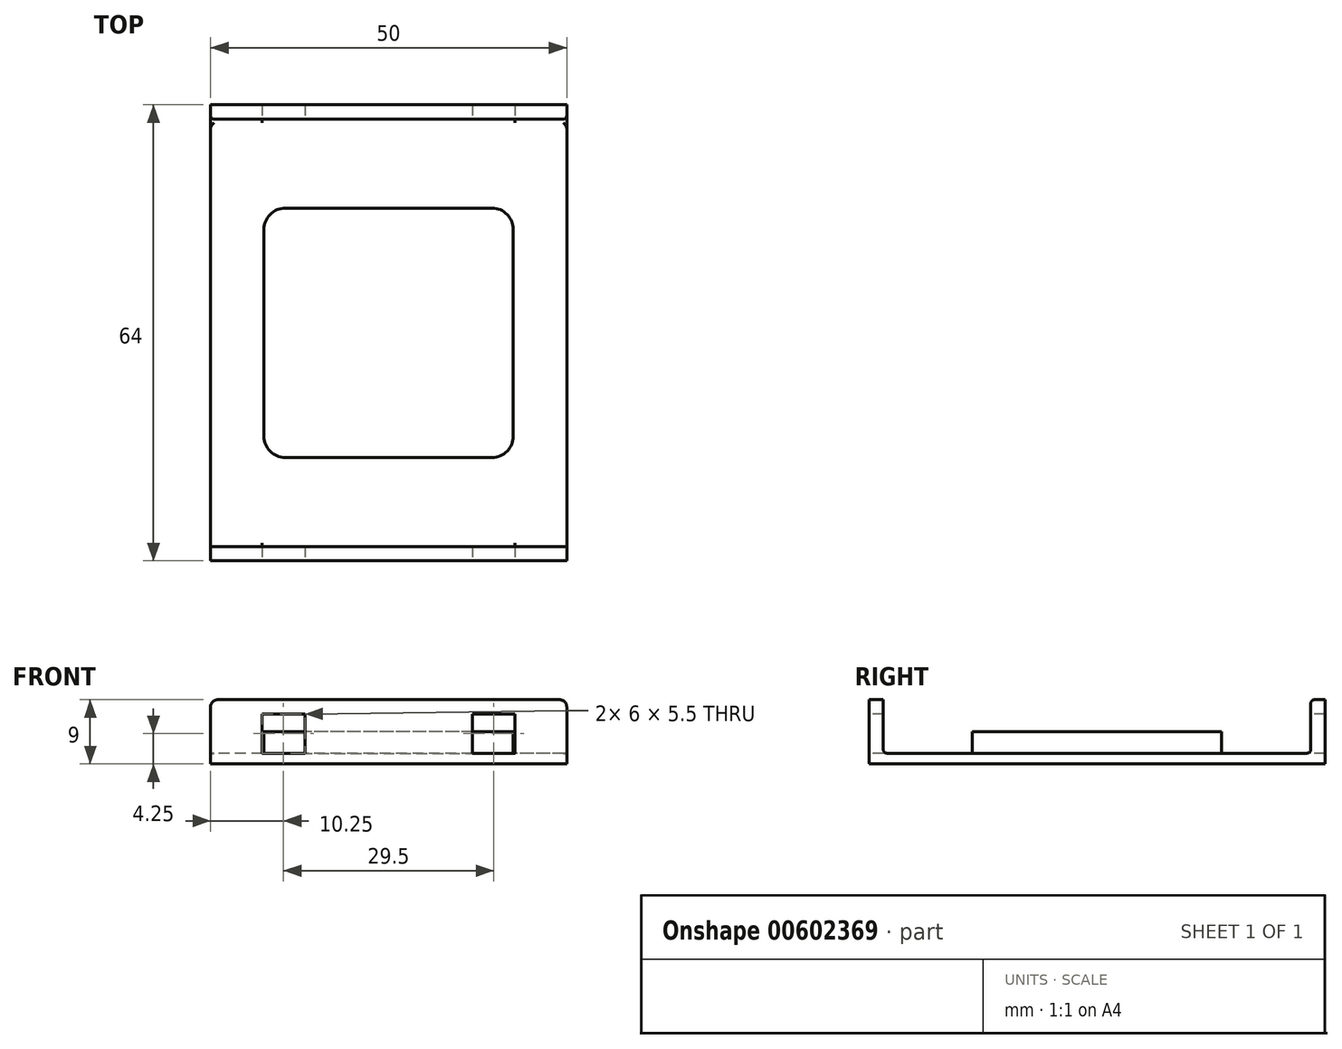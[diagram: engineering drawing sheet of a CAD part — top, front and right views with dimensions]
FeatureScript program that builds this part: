
annotation { "Feature Type Name" : "Feature", "Feature Type Description" : "" }
export const myFeature = defineFeature(function(context is Context, id is Id, definition is map)
    precondition{}
    {
        {
            var Q0;
            Q0=qCreatedBy(makeId("Top.planeOp"),FACE);
            var sketch = newSketch(context, id + "F0", { "sketchPlane" : qUnion([Q0])});
            skLineSegment(sketch, "E0.bottom", {"start": v(25, -30) * mm, "end": v(-25, -30) * mm});
            skLineSegment(sketch, "E0.top", {"start": v(25, 30) * mm, "end": v(-25, 30) * mm});
            skLineSegment(sketch, "E0.left", {"start": v(25, -30) * mm, "end": v(25, 30) * mm});
            skLineSegment(sketch, "E0.right", {"start": v(-25, -30) * mm, "end": v(-25, 30) * mm});
            skPoint(sketch, "E0.middle", {"position": v(0, 0) * mm});
            skSolve(sketch);
        }
        {
            var Q0;
            Q0=makeQuery(id+"F0.imprint","IMPRINT",FACE,{"disambiguationData":[TD([[makeQuery(id+"F0.imprint","IMPRINT",EDGE,{"derivedFrom":sQuery(id+"F0.wireOp",EDGE,"E0.bottom")}),-1.0]])]});
            extrude(context, id + "F1", {"entities" : qUnion([Q0]), "depth" : 1.5 * mm, "offsetDistance" : 25 * mm});
        }
        {
            var Q0;
            Q0=qCreatedBy(makeId("Top.planeOp"),FACE);
            var sketch = newSketch(context, id + "F2", { "sketchPlane" : qUnion([Q0])});
            skLineSegment(sketch, "E1.bottom", {"start": v(0, 32) * mm, "end": v(20, 32) * mm});
            skLineSegment(sketch, "E1.top", {"start": v(0, 30) * mm, "end": v(20, 30) * mm});
            skLineSegment(sketch, "E1.left", {"start": v(0, 32) * mm, "end": v(0, 30) * mm});
            skLineSegment(sketch, "E1.right", {"start": v(20, 32) * mm, "end": v(20, 30) * mm});
            skLineSegment(sketch, "E2.MirrorCS", {"start": v(-20, 32) * mm, "end": v(-20, 30) * mm});
            skLineSegment(sketch, "E3.MirrorCS", {"start": v(0, 32) * mm, "end": v(-20, 32) * mm});
            skLineSegment(sketch, "E4.MirrorCS", {"start": v(0, 30) * mm, "end": v(-20, 30) * mm});
            skLineSegment(sketch, "E5.MirrorCS", {"start": v(0, -32) * mm, "end": v(0, -30) * mm});
            skLineSegment(sketch, "E6.MirrorCS", {"start": v(-20, -32) * mm, "end": v(-20, -30) * mm});
            skLineSegment(sketch, "E7.MirrorCS", {"start": v(20, -32) * mm, "end": v(20, -30) * mm});
            skLineSegment(sketch, "E8.MirrorCS", {"start": v(0, -30) * mm, "end": v(-20, -30) * mm});
            skLineSegment(sketch, "E9.MirrorCS", {"start": v(0, -32) * mm, "end": v(-20, -32) * mm});
            skLineSegment(sketch, "E10.MirrorCS", {"start": v(0, -32) * mm, "end": v(20, -32) * mm});
            skLineSegment(sketch, "E11.MirrorCS", {"start": v(0, -30) * mm, "end": v(20, -30) * mm});
            skSolve(sketch);
        }
        {
            var Q0;
            Q0=qSketchRegion(id+"F2",true);
            extrude(context, id + "F3", {"entities" : qUnion([Q0]), "operationType" : NewBodyOperationType.ADD, "depth" : 9 * mm, "offsetDistance" : 25 * mm});
        }
        {
            var Q0;
            Q0=qCreatedBy(makeId("Front.planeOp"),FACE);
            var sketch = newSketch(context, id + "F4", { "sketchPlane" : qUnion([Q0])});
            skLineSegment(sketch, "E12.bottom", {"start": v(-17.75, 7) * mm, "end": v(-11.75, 7) * mm});
            skLineSegment(sketch, "E12.top", {"start": v(-17.75, 1.5) * mm, "end": v(-11.75, 1.5) * mm});
            skLineSegment(sketch, "E12.left", {"start": v(-17.75, 7) * mm, "end": v(-17.75, 1.5) * mm});
            skLineSegment(sketch, "E12.right", {"start": v(-11.75, 7) * mm, "end": v(-11.75, 1.5) * mm});
            skLineSegment(sketch, "E13.MirrorCS", {"start": v(17.75, 7) * mm, "end": v(11.75, 7) * mm});
            skLineSegment(sketch, "E14.MirrorCS", {"start": v(17.75, 7) * mm, "end": v(17.75, 1.5) * mm});
            skLineSegment(sketch, "E15.MirrorCS", {"start": v(17.75, 1.5) * mm, "end": v(11.75, 1.5) * mm});
            skLineSegment(sketch, "E16.MirrorCS", {"start": v(11.75, 7) * mm, "end": v(11.75, 1.5) * mm});
            skSolve(sketch);
        }
        {
            var Q0;
            Q0=qSketchRegion(id+"F4",true);
            extrude(context, id + "F5", {"entities" : qUnion([Q0]), "operationType" : NewBodyOperationType.REMOVE, "endBound" : BoundingType.SYMMETRIC, "oppositeDirection" : true, "depth" : 64 * mm, "offsetDistance" : 25 * mm});
        }
        {
            var Q0;
            Q0=qCreatedBy(makeId("Top.planeOp"),FACE);
            var sketch = newSketch(context, id + "F6", { "sketchPlane" : qUnion([Q0])});
            skLineSegment(sketch, "E17.bottom", {"start": v(17.5, -17.5) * mm, "end": v(-17.5, -17.5) * mm});
            skLineSegment(sketch, "E17.top", {"start": v(17.5, 17.5) * mm, "end": v(-17.5, 17.5) * mm});
            skLineSegment(sketch, "E17.left", {"start": v(17.5, -17.5) * mm, "end": v(17.5, 17.5) * mm});
            skLineSegment(sketch, "E17.right", {"start": v(-17.5, -17.5) * mm, "end": v(-17.5, 17.5) * mm});
            skPoint(sketch, "E17.middle", {"position": v(0, 0) * mm});
            skSolve(sketch);
        }
        {
            var Q0;
            Q0=qSketchRegion(id+"F6",true);
            extrude(context, id + "F7", {"entities" : qUnion([Q0]), "operationType" : NewBodyOperationType.ADD, "depth" : 4.5 * mm, "offsetDistance" : 25 * mm});
        }
        {
            var Q0;
            Q0=makeQuery(id+"F7.opExtrude","SWEPT_EDGE",EDGE,{"disambiguationData":[OSD([sQuery(id+"F6.wireOp",EDGE,"E17.bottom"),sQuery(id+"F6.wireOp",EDGE,"E17.left")])]});
            var Q1;
            Q1=makeQuery(id+"F7.opExtrude","SWEPT_EDGE",EDGE,{"disambiguationData":[OSD([sQuery(id+"F6.wireOp",EDGE,"E17.bottom"),sQuery(id+"F6.wireOp",EDGE,"E17.right")])]});
            var Q2;
            Q2=makeQuery(id+"F7.opExtrude","SWEPT_EDGE",EDGE,{"disambiguationData":[OSD([sQuery(id+"F6.wireOp",EDGE,"E17.top"),sQuery(id+"F6.wireOp",EDGE,"E17.right")])]});
            var Q3;
            Q3=makeQuery(id+"F7.opExtrude","SWEPT_EDGE",EDGE,{"disambiguationData":[OSD([sQuery(id+"F6.wireOp",EDGE,"E17.top"),sQuery(id+"F6.wireOp",EDGE,"E17.left")])]});
            fillet(context, id + "F8", {"entities" : qUnion([Q0, Q1, Q2, Q3]), "radius" : 3 * mm, "tangentPropagation" : true, "allowEdgeOverflow" : false});
        }
        {
            var Q0;
            Q0=makeQuery(id+"F3.opExtrude","SWEPT_FACE",FACE,{"disambiguationData":[OSD([sQuery(id+"F2.wireOp",EDGE,"E7.MirrorCS")])]});
            extrude(context, id + "F9", {"entities" : qUnion([Q0]), "operationType" : NewBodyOperationType.ADD, "depth" : 5 * mm, "offsetDistance" : 25 * mm});
        }
        {
            var Q0;
            Q0=makeQuery(id+"F3.opExtrude","SWEPT_FACE",FACE,{"disambiguationData":[OSD([sQuery(id+"F2.wireOp",EDGE,"E2.MirrorCS")])]});
            extrude(context, id + "F10", {"entities" : qUnion([Q0]), "operationType" : NewBodyOperationType.ADD, "depth" : 5 * mm, "offsetDistance" : 25 * mm});
        }
        {
            var Q0;
            Q0=makeQuery(id+"F3.opExtrude","SWEPT_FACE",FACE,{"disambiguationData":[OSD([sQuery(id+"F2.wireOp",EDGE,"E6.MirrorCS")])]});
            extrude(context, id + "F11", {"entities" : qUnion([Q0]), "operationType" : NewBodyOperationType.ADD, "depth" : 5 * mm, "offsetDistance" : 25 * mm});
        }
        {
            var Q0;
            Q0=makeQuery(id+"F3.opExtrude","SWEPT_FACE",FACE,{"disambiguationData":[OSD([sQuery(id+"F2.wireOp",EDGE,"E1.right")])]});
            extrude(context, id + "F12", {"entities" : qUnion([Q0]), "operationType" : NewBodyOperationType.ADD, "depth" : 5 * mm, "offsetDistance" : 25 * mm});
        }
        {
            var Q0;
            {var subQ0=sQuery(id+"F2.wireOp",EDGE,"E1.right");Q0=makeQuery(id+"F12.opExtrude","CAP_EDGE",EDGE,{"disambiguationData":[OSD([subQ0]),TDD([makeQuery(id+"F3.opExtrude","CAP_EDGE",EDGE,{"disambiguationData":[OSD([subQ0])],"isStart":false})])],"isStart":false});}
            var Q1;
            {var subQ0=sQuery(id+"F2.wireOp",EDGE,"E6.MirrorCS");Q1=makeQuery(id+"F11.opExtrude","CAP_EDGE",EDGE,{"disambiguationData":[OSD([subQ0]),TDD([makeQuery(id+"F3.opExtrude","CAP_EDGE",EDGE,{"disambiguationData":[OSD([subQ0])],"isStart":false})])],"isStart":false});}
            var Q2;
            {var subQ0=sQuery(id+"F2.wireOp",EDGE,"E2.MirrorCS");Q2=makeQuery(id+"F10.opExtrude","CAP_EDGE",EDGE,{"disambiguationData":[OSD([subQ0]),TDD([makeQuery(id+"F3.opExtrude","CAP_EDGE",EDGE,{"disambiguationData":[OSD([subQ0])],"isStart":false})])],"isStart":false});}
            var Q3;
            {var subQ0=sQuery(id+"F2.wireOp",EDGE,"E7.MirrorCS");Q3=makeQuery(id+"F9.opExtrude","CAP_EDGE",EDGE,{"disambiguationData":[OSD([subQ0]),TDD([makeQuery(id+"F3.opExtrude","CAP_EDGE",EDGE,{"disambiguationData":[OSD([subQ0])],"isStart":false})])],"isStart":false});}
            fillet(context, id + "F13", {"entities" : qUnion([Q0, Q1, Q2, Q3]), "radius" : 1 * mm, "tangentPropagation" : true, "allowEdgeOverflow" : false});
        }
        {
            var Q0;
            {var subQ0=makeQuery(id+"F3.opExtrude","SWEPT_FACE",FACE,{"disambiguationData":[OSD([sQuery(id+"F2.wireOp",EDGE,"E1.top"),sQuery(id+"F2.wireOp",EDGE,"E4.MirrorCS")])]});var subQ1=makeQuery(id+"F3.opExtrude","SWEPT_FACE",FACE,{"disambiguationData":[OSD([sQuery(id+"F2.wireOp",EDGE,"E2.MirrorCS")])]});var subQ2=sQuery(id+"F0.wireOp",EDGE,"E0.top");var subQ3=makeQuery(id+"F1.opExtrude","SWEPT_FACE",FACE,{"disambiguationData":[OSD([subQ2])]});var subQ4=sQuery(id+"F0.wireOp",EDGE,"E0.right");var subQ5=makeQuery(id+"F1.opExtrude","CAP_FACE",FACE,{"disambiguationData":[OSD([sQuery(id+"F0.wireOp",EDGE,"E0.bottom"),subQ2,sQuery(id+"F0.wireOp",EDGE,"E0.left"),subQ4])],"isStart":false});var subQ6=makeQuery(id+"F1.opExtrude","CAP_EDGE",EDGE,{"disambiguationData":[OSD([subQ2])],"isStart":false});Q0=makeQuery(id+"F10.boolean.opBoolean","MERGE",EDGE,{"derivedFrom":[makeQuery(id+"F3.boolean.opBoolean","SPLIT",EDGE,{"disambiguationData":[topologyDisambiguationEdgeConnected([subQ5,subQ3]),TD([makeQuery(id+"F1.opExtrude","SWEPT_FACE",FACE,{"disambiguationData":[OSD([subQ4])]})])],"derivedFrom":subQ6}),makeQuery(id+"F5.boolean.opBoolean","SPLIT",EDGE,{"disambiguationData":[TD([subQ1])],"derivedFrom":makeQuery(id+"F3.boolean.opBoolean","SPLIT",EDGE,{"disambiguationData":[topologyDisambiguationEdgeConnected([subQ5,subQ0])],"derivedFrom":subQ6})})]});}
            var Q1;
            {var subQ0=makeQuery(id+"F3.opExtrude","SWEPT_FACE",FACE,{"disambiguationData":[OSD([sQuery(id+"F2.wireOp",EDGE,"E1.top"),sQuery(id+"F2.wireOp",EDGE,"E4.MirrorCS")])]});var subQ1=sQuery(id+"F0.wireOp",EDGE,"E0.top");var subQ2=makeQuery(id+"F1.opExtrude","CAP_FACE",FACE,{"disambiguationData":[OSD([sQuery(id+"F0.wireOp",EDGE,"E0.bottom"),subQ1,sQuery(id+"F0.wireOp",EDGE,"E0.left"),sQuery(id+"F0.wireOp",EDGE,"E0.right")])],"isStart":false});Q1=makeQuery(id+"F5.boolean.opBoolean","SPLIT",EDGE,{"disambiguationData":[TD([makeQuery(id+"F5.opExtrude","SWEPT_FACE",FACE,{"disambiguationData":[OSD([sQuery(id+"F4.wireOp",EDGE,"E12.right")])]})])],"derivedFrom":makeQuery(id+"F3.boolean.opBoolean","SPLIT",EDGE,{"disambiguationData":[topologyDisambiguationEdgeConnected([subQ2,subQ0])],"derivedFrom":makeQuery(id+"F1.opExtrude","CAP_EDGE",EDGE,{"disambiguationData":[OSD([subQ1])],"isStart":false})})});}
            var Q2;
            {var subQ0=makeQuery(id+"F3.opExtrude","SWEPT_FACE",FACE,{"disambiguationData":[OSD([sQuery(id+"F2.wireOp",EDGE,"E1.top"),sQuery(id+"F2.wireOp",EDGE,"E4.MirrorCS")])]});var subQ1=sQuery(id+"F0.wireOp",EDGE,"E0.top");var subQ2=makeQuery(id+"F1.opExtrude","SWEPT_FACE",FACE,{"disambiguationData":[OSD([subQ1])]});var subQ3=makeQuery(id+"F3.opExtrude","SWEPT_FACE",FACE,{"disambiguationData":[OSD([sQuery(id+"F2.wireOp",EDGE,"E1.right")])]});var subQ4=sQuery(id+"F0.wireOp",EDGE,"E0.left");var subQ5=makeQuery(id+"F1.opExtrude","CAP_FACE",FACE,{"disambiguationData":[OSD([sQuery(id+"F0.wireOp",EDGE,"E0.bottom"),subQ1,subQ4,sQuery(id+"F0.wireOp",EDGE,"E0.right")])],"isStart":false});var subQ6=makeQuery(id+"F1.opExtrude","CAP_EDGE",EDGE,{"disambiguationData":[OSD([subQ1])],"isStart":false});Q2=makeQuery(id+"F12.boolean.opBoolean","MERGE",EDGE,{"derivedFrom":[makeQuery(id+"F3.boolean.opBoolean","SPLIT",EDGE,{"disambiguationData":[topologyDisambiguationEdgeConnected([subQ5,subQ2]),TD([makeQuery(id+"F1.opExtrude","SWEPT_FACE",FACE,{"disambiguationData":[OSD([subQ4])]})])],"derivedFrom":subQ6}),makeQuery(id+"F5.boolean.opBoolean","SPLIT",EDGE,{"disambiguationData":[TD([subQ3])],"derivedFrom":makeQuery(id+"F3.boolean.opBoolean","SPLIT",EDGE,{"disambiguationData":[topologyDisambiguationEdgeConnected([subQ5,subQ0])],"derivedFrom":subQ6})})]});}
            var Q3;
            {var subQ0=makeQuery(id+"F3.opExtrude","SWEPT_FACE",FACE,{"disambiguationData":[OSD([sQuery(id+"F2.wireOp",EDGE,"E8.MirrorCS"),sQuery(id+"F2.wireOp",EDGE,"E11.MirrorCS")])]});var subQ1=sQuery(id+"F0.wireOp",EDGE,"E0.bottom");var subQ2=makeQuery(id+"F1.opExtrude","SWEPT_FACE",FACE,{"disambiguationData":[OSD([subQ1])]});var subQ3=makeQuery(id+"F3.opExtrude","SWEPT_FACE",FACE,{"disambiguationData":[OSD([sQuery(id+"F2.wireOp",EDGE,"E6.MirrorCS")])]});var subQ4=sQuery(id+"F0.wireOp",EDGE,"E0.right");var subQ5=makeQuery(id+"F1.opExtrude","CAP_FACE",FACE,{"disambiguationData":[OSD([subQ1,sQuery(id+"F0.wireOp",EDGE,"E0.top"),sQuery(id+"F0.wireOp",EDGE,"E0.left"),subQ4])],"isStart":false});var subQ6=makeQuery(id+"F1.opExtrude","CAP_EDGE",EDGE,{"disambiguationData":[OSD([subQ1])],"isStart":false});Q3=makeQuery(id+"F11.boolean.opBoolean","MERGE",EDGE,{"derivedFrom":[makeQuery(id+"F3.boolean.opBoolean","SPLIT",EDGE,{"disambiguationData":[topologyDisambiguationEdgeConnected([subQ2,subQ5]),TD([makeQuery(id+"F1.opExtrude","SWEPT_FACE",FACE,{"disambiguationData":[OSD([subQ4])]})])],"derivedFrom":subQ6}),makeQuery(id+"F5.boolean.opBoolean","SPLIT",EDGE,{"disambiguationData":[TD([subQ3])],"derivedFrom":makeQuery(id+"F3.boolean.opBoolean","SPLIT",EDGE,{"disambiguationData":[topologyDisambiguationEdgeConnected([subQ5,subQ0])],"derivedFrom":subQ6})})]});}
            var Q4;
            {var subQ0=makeQuery(id+"F3.opExtrude","SWEPT_FACE",FACE,{"disambiguationData":[OSD([sQuery(id+"F2.wireOp",EDGE,"E8.MirrorCS"),sQuery(id+"F2.wireOp",EDGE,"E11.MirrorCS")])]});var subQ1=sQuery(id+"F0.wireOp",EDGE,"E0.bottom");var subQ2=makeQuery(id+"F1.opExtrude","CAP_FACE",FACE,{"disambiguationData":[OSD([subQ1,sQuery(id+"F0.wireOp",EDGE,"E0.top"),sQuery(id+"F0.wireOp",EDGE,"E0.left"),sQuery(id+"F0.wireOp",EDGE,"E0.right")])],"isStart":false});Q4=makeQuery(id+"F5.boolean.opBoolean","SPLIT",EDGE,{"disambiguationData":[TD([makeQuery(id+"F5.opExtrude","SWEPT_FACE",FACE,{"disambiguationData":[OSD([sQuery(id+"F4.wireOp",EDGE,"E12.right")])]})])],"derivedFrom":makeQuery(id+"F3.boolean.opBoolean","SPLIT",EDGE,{"disambiguationData":[topologyDisambiguationEdgeConnected([subQ2,subQ0])],"derivedFrom":makeQuery(id+"F1.opExtrude","CAP_EDGE",EDGE,{"disambiguationData":[OSD([subQ1])],"isStart":false})})});}
            var Q5;
            {var subQ0=makeQuery(id+"F3.opExtrude","SWEPT_FACE",FACE,{"disambiguationData":[OSD([sQuery(id+"F2.wireOp",EDGE,"E8.MirrorCS"),sQuery(id+"F2.wireOp",EDGE,"E11.MirrorCS")])]});var subQ1=sQuery(id+"F0.wireOp",EDGE,"E0.bottom");var subQ2=makeQuery(id+"F1.opExtrude","SWEPT_FACE",FACE,{"disambiguationData":[OSD([subQ1])]});var subQ3=makeQuery(id+"F3.opExtrude","SWEPT_FACE",FACE,{"disambiguationData":[OSD([sQuery(id+"F2.wireOp",EDGE,"E7.MirrorCS")])]});var subQ4=sQuery(id+"F0.wireOp",EDGE,"E0.left");var subQ5=makeQuery(id+"F1.opExtrude","CAP_FACE",FACE,{"disambiguationData":[OSD([subQ1,sQuery(id+"F0.wireOp",EDGE,"E0.top"),subQ4,sQuery(id+"F0.wireOp",EDGE,"E0.right")])],"isStart":false});var subQ6=makeQuery(id+"F1.opExtrude","CAP_EDGE",EDGE,{"disambiguationData":[OSD([subQ1])],"isStart":false});Q5=makeQuery(id+"F9.boolean.opBoolean","MERGE",EDGE,{"derivedFrom":[makeQuery(id+"F3.boolean.opBoolean","SPLIT",EDGE,{"disambiguationData":[topologyDisambiguationEdgeConnected([subQ2,subQ5]),TD([makeQuery(id+"F1.opExtrude","SWEPT_FACE",FACE,{"disambiguationData":[OSD([subQ4])]})])],"derivedFrom":subQ6}),makeQuery(id+"F5.boolean.opBoolean","SPLIT",EDGE,{"disambiguationData":[TD([subQ3])],"derivedFrom":makeQuery(id+"F3.boolean.opBoolean","SPLIT",EDGE,{"disambiguationData":[topologyDisambiguationEdgeConnected([subQ5,subQ0])],"derivedFrom":subQ6})})]});}
            var Q6;
            {var subQ0=sQuery(id+"F2.wireOp",EDGE,"E1.right");var subQ1=sQuery(id+"F2.wireOp",EDGE,"E1.top");var subQ2=sQuery(id+"F2.wireOp",EDGE,"E4.MirrorCS");var subQ3=sQuery(id+"F2.wireOp",EDGE,"E2.MirrorCS");Q6=makeQuery(id+"F12.boolean.opBoolean","MERGE",EDGE,{"derivedFrom":[makeQuery(id+"F10.boolean.opBoolean","MERGE",EDGE,{"derivedFrom":[makeQuery(id+"F3.opExtrude","CAP_EDGE",EDGE,{"disambiguationData":[OSD([subQ1,subQ2])],"isStart":false}),makeQuery(id+"F10.opExtrude","SWEPT_EDGE",EDGE,{"disambiguationData":[OSD([subQ3,subQ2]),TDD([makeQuery(id+"F3.opExtrude","CAP_VERTEX",VERTEX,{"disambiguationData":[OSD([subQ3,subQ2])],"isStart":false})])]})]}),makeQuery(id+"F12.opExtrude","SWEPT_EDGE",EDGE,{"disambiguationData":[OSD([subQ1,subQ0]),TDD([makeQuery(id+"F3.opExtrude","CAP_VERTEX",VERTEX,{"disambiguationData":[OSD([subQ1,subQ0])],"isStart":false})])]})]});}
            fillet(context, id + "F14", {"entities" : qUnion([Q0, Q1, Q2, Q3, Q4, Q5, Q6]), "radius" : 0.5 * mm, "tangentPropagation" : true, "allowEdgeOverflow" : false});
        }
    });
